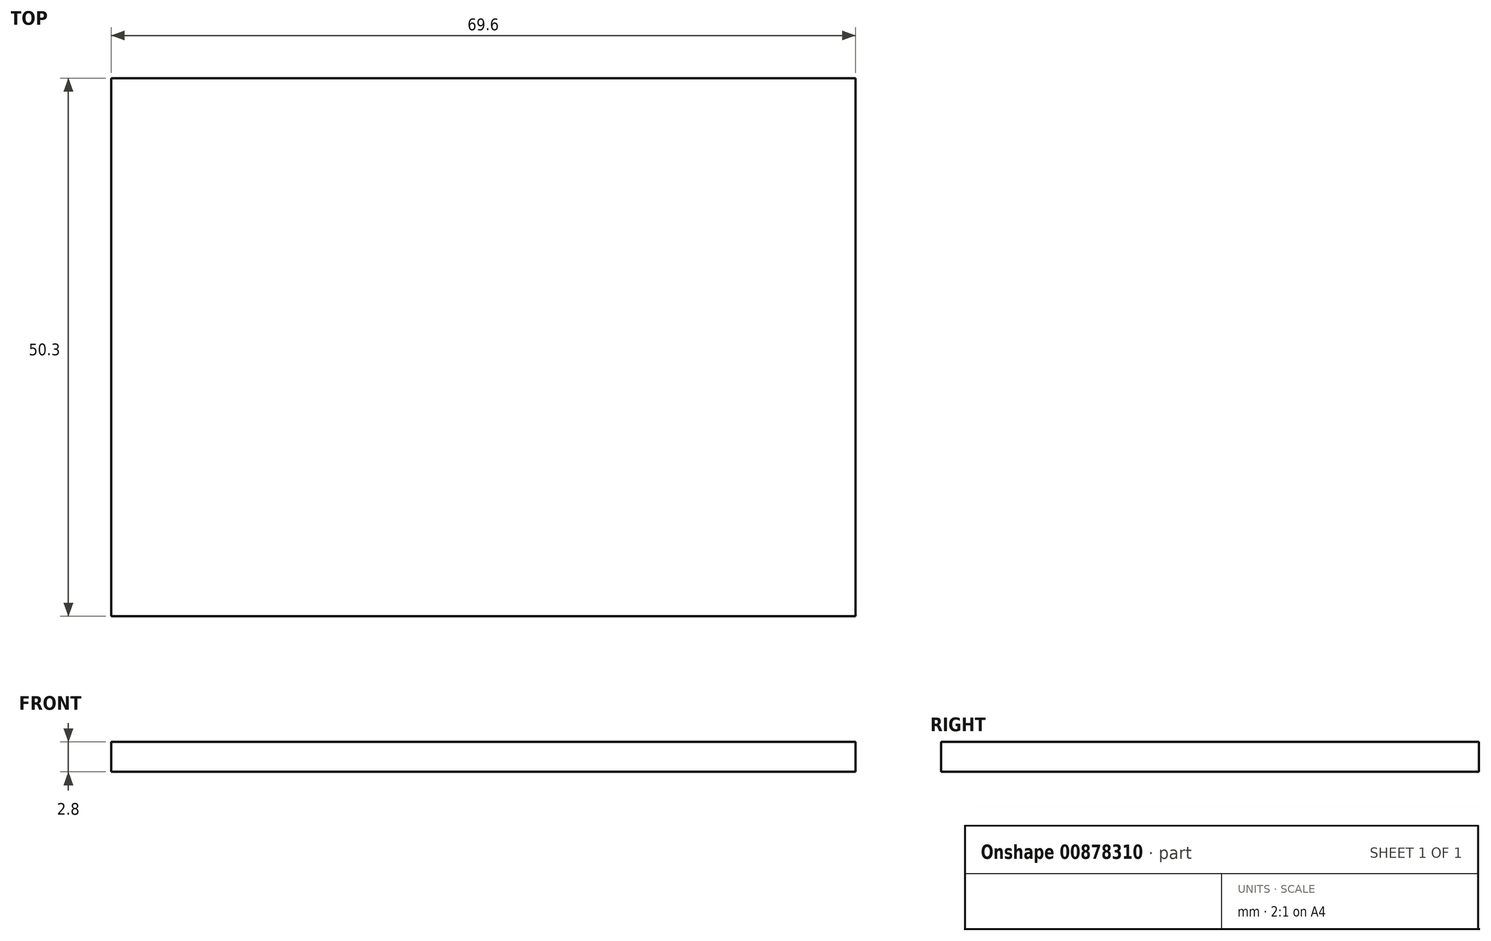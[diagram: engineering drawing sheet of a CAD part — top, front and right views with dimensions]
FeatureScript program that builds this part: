
annotation { "Feature Type Name" : "Feature", "Feature Type Description" : "" }
export const myFeature = defineFeature(function(context is Context, id is Id, definition is map)
    precondition{}
    {
        {
            var Q0;
            Q0=qCreatedBy(makeId("Top.planeOp"),FACE);
            var sketch = newSketch(context, id + "F0", { "sketchPlane" : qUnion([Q0])});
            skLineSegment(sketch, "E0.bottom", {"start": v(-29.16, 29.44) * mm, "end": v(40.44, 29.44) * mm});
            skLineSegment(sketch, "E0.top", {"start": v(-29.16, -20.86) * mm, "end": v(40.44, -20.86) * mm});
            skLineSegment(sketch, "E0.left", {"start": v(-29.16, 29.44) * mm, "end": v(-29.16, -20.86) * mm});
            skLineSegment(sketch, "E0.right", {"start": v(40.44, 29.44) * mm, "end": v(40.44, -20.86) * mm});
            skSolve(sketch);
        }
        {
            var Q0;
            Q0=makeQuery(id+"F0.imprint","IMPRINT",FACE,{"disambiguationData":[TD([[makeQuery(id+"F0.imprint","IMPRINT",EDGE,{"derivedFrom":sQuery(id+"F0.wireOp",EDGE,"E0.bottom")}),-1.0]])]});
            extrude(context, id + "F1", {"entities" : qUnion([Q0]), "depth" : 2.8 * mm, "offsetDistance" : 25 * mm});
        }
    });
